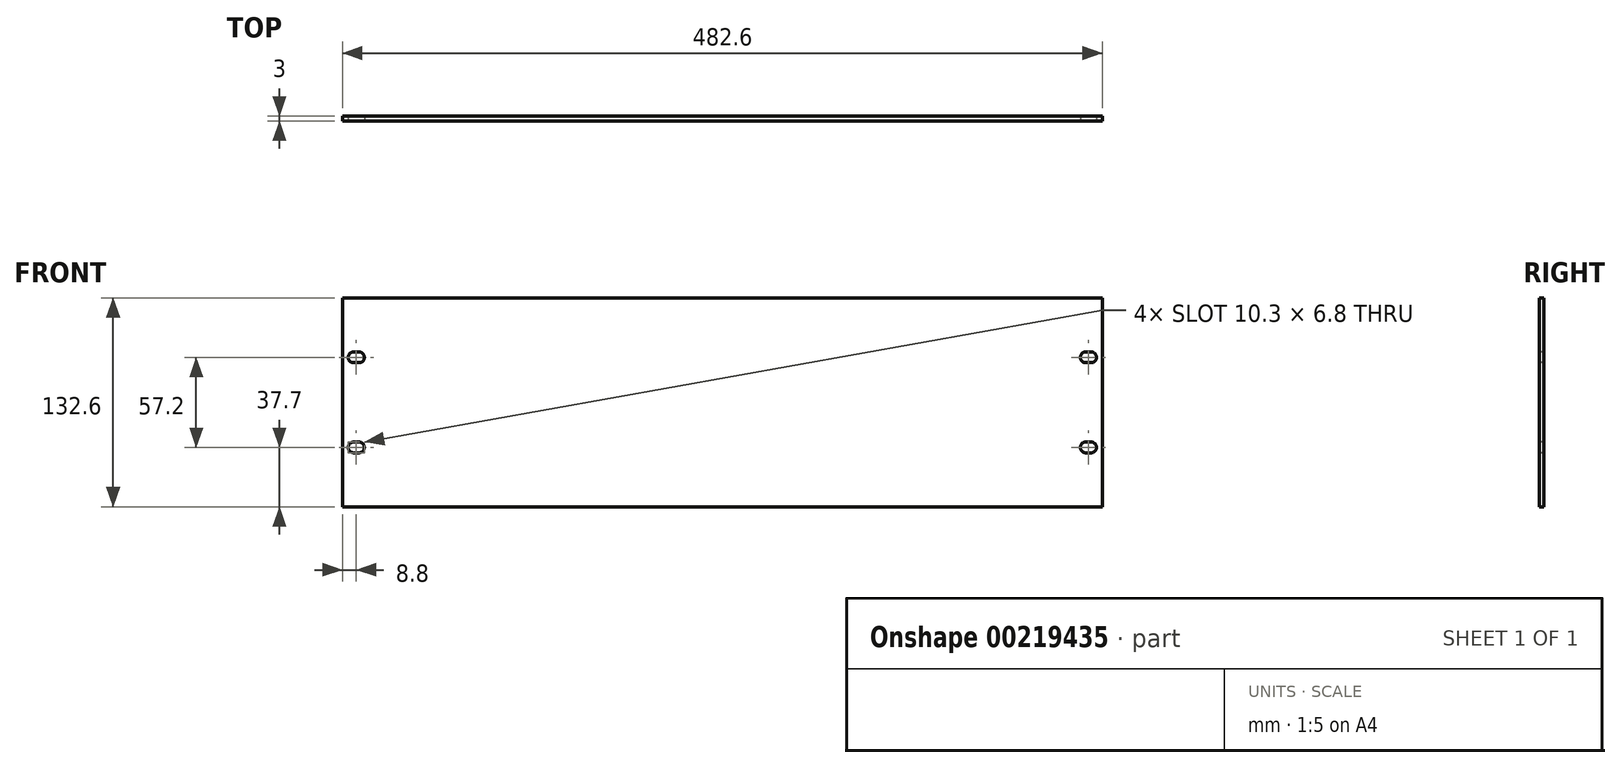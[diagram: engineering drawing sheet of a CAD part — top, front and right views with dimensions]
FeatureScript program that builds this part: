
annotation { "Feature Type Name" : "Feature", "Feature Type Description" : "" }
export const myFeature = defineFeature(function(context is Context, id is Id, definition is map)
    precondition{}
    {
        {
            var Q0;
            Q0=qCreatedBy(makeId("Front.planeOp"),FACE);
            var sketch = newSketch(context, id + "F0", { "sketchPlane" : qUnion([Q0])});
            skLineSegment(sketch, "E0.bottom", {"start": v(-241.3, 66.3) * mm, "end": v(241.3, 66.3) * mm});
            skLineSegment(sketch, "E0.top", {"start": v(-241.3, -66.3) * mm, "end": v(241.3, -66.3) * mm});
            skLineSegment(sketch, "E0.left", {"start": v(-241.3, 66.3) * mm, "end": v(-241.3, -66.3) * mm});
            skLineSegment(sketch, "E0.right", {"start": v(241.3, 66.3) * mm, "end": v(241.3, -66.3) * mm});
            skPoint(sketch, "E0.middle", {"position": v(0, 0) * mm});
            skSolve(sketch);
        }
        {
            var Q0;
            Q0=qSketchRegion(id+"F0",true);
            extrude(context, id + "F1", {"entities" : qUnion([Q0]), "oppositeDirection" : true, "depth" : 3 * mm});
        }
        {
            var Q0;
            Q0=makeQuery(id+"F1.opExtrude","CAP_FACE",FACE,{"disambiguationData":[OSD([sQuery(id+"F0.wireOp",EDGE,"E0.bottom"),sQuery(id+"F0.wireOp",EDGE,"E0.top"),sQuery(id+"F0.wireOp",EDGE,"E0.left"),sQuery(id+"F0.wireOp",EDGE,"E0.right")])],"isStart":true});
            var sketch = newSketch(context, id + "F2", { "sketchPlane" : qUnion([Q0])});
            skLineSegment(sketch, "E1.bottom", {"start": v(-230.75, 25.2) * mm, "end": v(-234.25, 25.2) * mm});
            skLineSegment(sketch, "E1.top", {"start": v(-230.75, 32) * mm, "end": v(-234.25, 32) * mm});
            skLineSegment(sketch, "E1.left", {"start": v(-230.75, 25.2) * mm, "end": v(-230.75, 32) * mm});
            skLineSegment(sketch, "E1.right", {"start": v(-234.25, 25.2) * mm, "end": v(-234.25, 32) * mm});
            skPoint(sketch, "E1.middle", {"position": v(-232.5, 28.6) * mm});
            skArc(sketch, "E2", {"start": v(-230.75, 25.2) * mm, "mid": v(-227.35, 28.6) * mm, "end": v(-230.75, 32) * mm});
            skArc(sketch, "E3", {"start": v(-234.25, 32) * mm, "mid": v(-237.65, 28.6) * mm, "end": v(-234.25, 25.2) * mm});
            skSolve(sketch);
        }
        {
            var Q0;
            Q0=makeQuery(id+"F2.imprint","IMPRINT",FACE,{"disambiguationData":[TD([[makeQuery(id+"F2.imprint","IMPRINT",EDGE,{"derivedFrom":sQuery(id+"F2.wireOp",EDGE,"E1.bottom")}),1.0]])]});
            var sketch = newSketch(context, id + "F3", { "sketchPlane" : qUnion([Q0])});
            skLineSegment(sketch, "E4.bottom", {"start": v(-230.75, -32) * mm, "end": v(-234.25, -32) * mm});
            skLineSegment(sketch, "E4.top", {"start": v(-230.75, -25.2) * mm, "end": v(-234.25, -25.2) * mm});
            skLineSegment(sketch, "E4.left", {"start": v(-230.75, -32) * mm, "end": v(-230.75, -25.2) * mm});
            skLineSegment(sketch, "E4.right", {"start": v(-234.25, -32) * mm, "end": v(-234.25, -25.2) * mm});
            skPoint(sketch, "E4.middle", {"position": v(-232.5, -28.6) * mm});
            skArc(sketch, "E5", {"start": v(-230.75, -32) * mm, "mid": v(-227.35, -28.6) * mm, "end": v(-230.75, -25.2) * mm});
            skArc(sketch, "E6", {"start": v(-234.25, -25.2) * mm, "mid": v(-237.65, -28.6) * mm, "end": v(-234.25, -32) * mm});
            skSolve(sketch);
        }
        {
            var Q0;
            Q0=makeQuery(id+"F2.imprint","IMPRINT",FACE,{"disambiguationData":[TD([[makeQuery(id+"F2.imprint","IMPRINT",EDGE,{"derivedFrom":sQuery(id+"F2.wireOp",EDGE,"E1.bottom")}),1.0]])]});
            var sketch = newSketch(context, id + "F4", { "sketchPlane" : qUnion([Q0])});
            skLineSegment(sketch, "E7.bottom", {"start": v(234.25, 32) * mm, "end": v(230.75, 32) * mm});
            skLineSegment(sketch, "E7.top", {"start": v(234.25, 25.2) * mm, "end": v(230.75, 25.2) * mm});
            skLineSegment(sketch, "E7.left", {"start": v(234.25, 32) * mm, "end": v(234.25, 25.2) * mm});
            skLineSegment(sketch, "E7.right", {"start": v(230.75, 32) * mm, "end": v(230.75, 25.2) * mm});
            skPoint(sketch, "E7.middle", {"position": v(232.5, 28.6) * mm});
            skArc(sketch, "E8", {"start": v(234.25, 25.2) * mm, "mid": v(237.65, 28.6) * mm, "end": v(234.25, 32) * mm});
            skArc(sketch, "E9", {"start": v(230.75, 32) * mm, "mid": v(227.35, 28.6) * mm, "end": v(230.75, 25.2) * mm});
            skSolve(sketch);
        }
        {
            var Q0;
            Q0=makeQuery(id+"F2.imprint","IMPRINT",FACE,{"disambiguationData":[TD([[makeQuery(id+"F2.imprint","IMPRINT",EDGE,{"derivedFrom":sQuery(id+"F2.wireOp",EDGE,"E1.bottom")}),1.0]])]});
            var sketch = newSketch(context, id + "F5", { "sketchPlane" : qUnion([Q0])});
            skLineSegment(sketch, "E10.bottom", {"start": v(234.25, -32) * mm, "end": v(230.75, -32) * mm});
            skLineSegment(sketch, "E10.top", {"start": v(234.25, -25.2) * mm, "end": v(230.75, -25.2) * mm});
            skLineSegment(sketch, "E10.left", {"start": v(234.25, -32) * mm, "end": v(234.25, -25.2) * mm});
            skLineSegment(sketch, "E10.right", {"start": v(230.75, -32) * mm, "end": v(230.75, -25.2) * mm});
            skPoint(sketch, "E10.middle", {"position": v(232.5, -28.6) * mm});
            skArc(sketch, "E11", {"start": v(230.75, -25.2) * mm, "mid": v(227.35, -28.6) * mm, "end": v(230.75, -32) * mm});
            skArc(sketch, "E12", {"start": v(234.25, -32) * mm, "mid": v(237.65, -28.6) * mm, "end": v(234.25, -25.2) * mm});
            skSolve(sketch);
        }
        {
            var Q0;
            Q0=qSketchRegion(id+"F2",true);
            var Q1;
            Q1=qSketchRegion(id+"F3",true);
            var Q2;
            Q2=qSketchRegion(id+"F4",true);
            var Q3;
            Q3=qSketchRegion(id+"F5",true);
            extrude(context, id + "F6", {"entities" : qUnion([Q0, Q1, Q2, Q3]), "operationType" : NewBodyOperationType.REMOVE, "oppositeDirection" : true, "depth" : 3 * mm});
        }
    });
